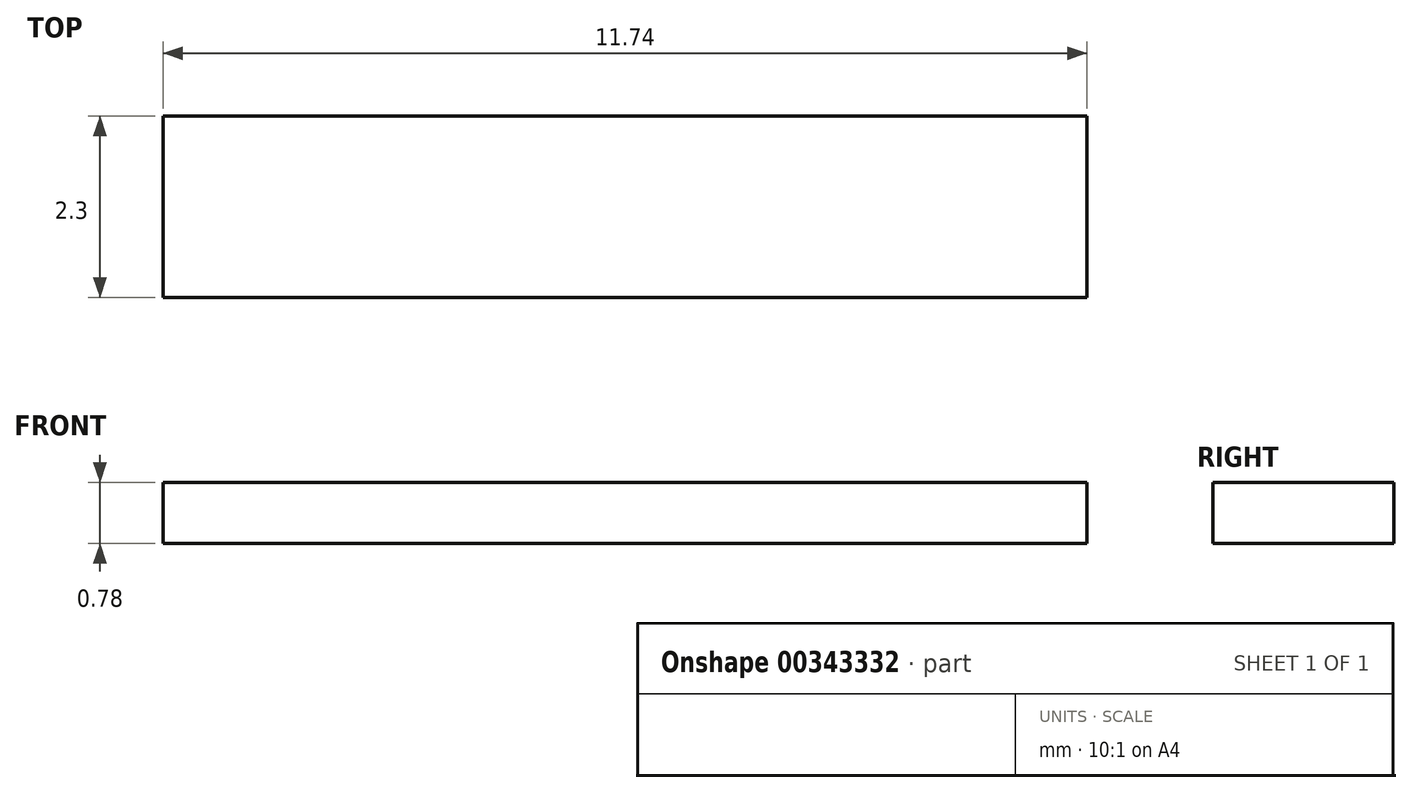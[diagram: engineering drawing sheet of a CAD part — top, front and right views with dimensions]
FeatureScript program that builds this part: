
annotation { "Feature Type Name" : "Feature", "Feature Type Description" : "" }
export const myFeature = defineFeature(function(context is Context, id is Id, definition is map)
    precondition{}
    {
        {
            var Q0;
            Q0=qCreatedBy(makeId("Top.planeOp"),FACE);
            var sketch = newSketch(context, id + "F0", { "sketchPlane" : qUnion([Q0])});
            skLineSegment(sketch, "E0.bottom", {"start": v(-5.87, 1.15) * mm, "end": v(5.87, 1.15) * mm});
            skLineSegment(sketch, "E0.top", {"start": v(-5.87, -1.15) * mm, "end": v(5.87, -1.15) * mm});
            skLineSegment(sketch, "E0.left", {"start": v(-5.87, 1.15) * mm, "end": v(-5.87, -1.15) * mm});
            skLineSegment(sketch, "E0.right", {"start": v(5.87, 1.15) * mm, "end": v(5.87, -1.15) * mm});
            skPoint(sketch, "E0.middle", {"position": v(0, 0) * mm});
            skSolve(sketch);
        }
        {
            var Q0;
            Q0 = qSketchRegion(id + "F0", true);
            extrude(context, id + "F1", {"entities" : qUnion([Q0]), "depth" : .780 * mm});
        }
    });
